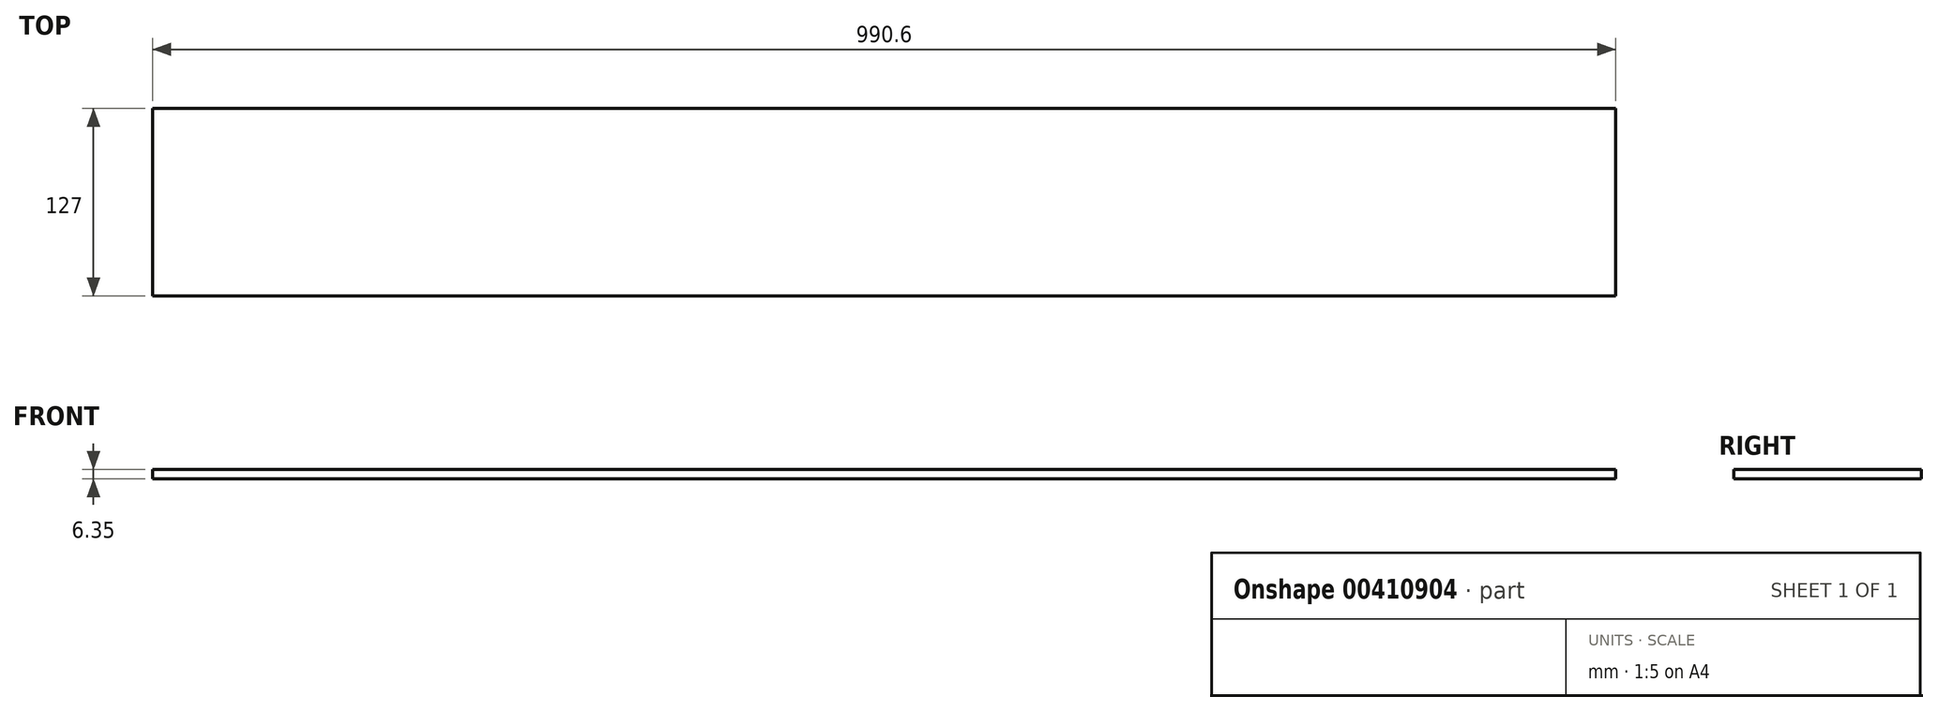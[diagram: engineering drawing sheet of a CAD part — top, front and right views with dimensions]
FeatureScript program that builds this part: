
annotation { "Feature Type Name" : "Feature", "Feature Type Description" : "" }
export const myFeature = defineFeature(function(context is Context, id is Id, definition is map)
    precondition{}
    {
        {
            var Q0;
            Q0=qCreatedBy(makeId("Top.planeOp"),FACE);
            var sketch = newSketch(context, id + "F0", { "sketchPlane" : qUnion([Q0])});
            skLineSegment(sketch, "E0.bottom", {"start": v(495.3, -63.5) * mm, "end": v(-495.3, -63.5) * mm});
            skLineSegment(sketch, "E0.top", {"start": v(495.3, 63.5) * mm, "end": v(-495.3, 63.5) * mm});
            skLineSegment(sketch, "E0.left", {"start": v(495.3, -63.5) * mm, "end": v(495.3, 63.5) * mm});
            skLineSegment(sketch, "E0.right", {"start": v(-495.3, -63.5) * mm, "end": v(-495.3, 63.5) * mm});
            skPoint(sketch, "E0.middle", {"position": v(0, 0) * mm});
            skSolve(sketch);
        }
        {
            var Q0;
            Q0 = qSketchRegion(id + "F0", true);
            extrude(context, id + "F1", {"entities" : qUnion([Q0]), "depth" : 6.35 * mm});
        }
    });
